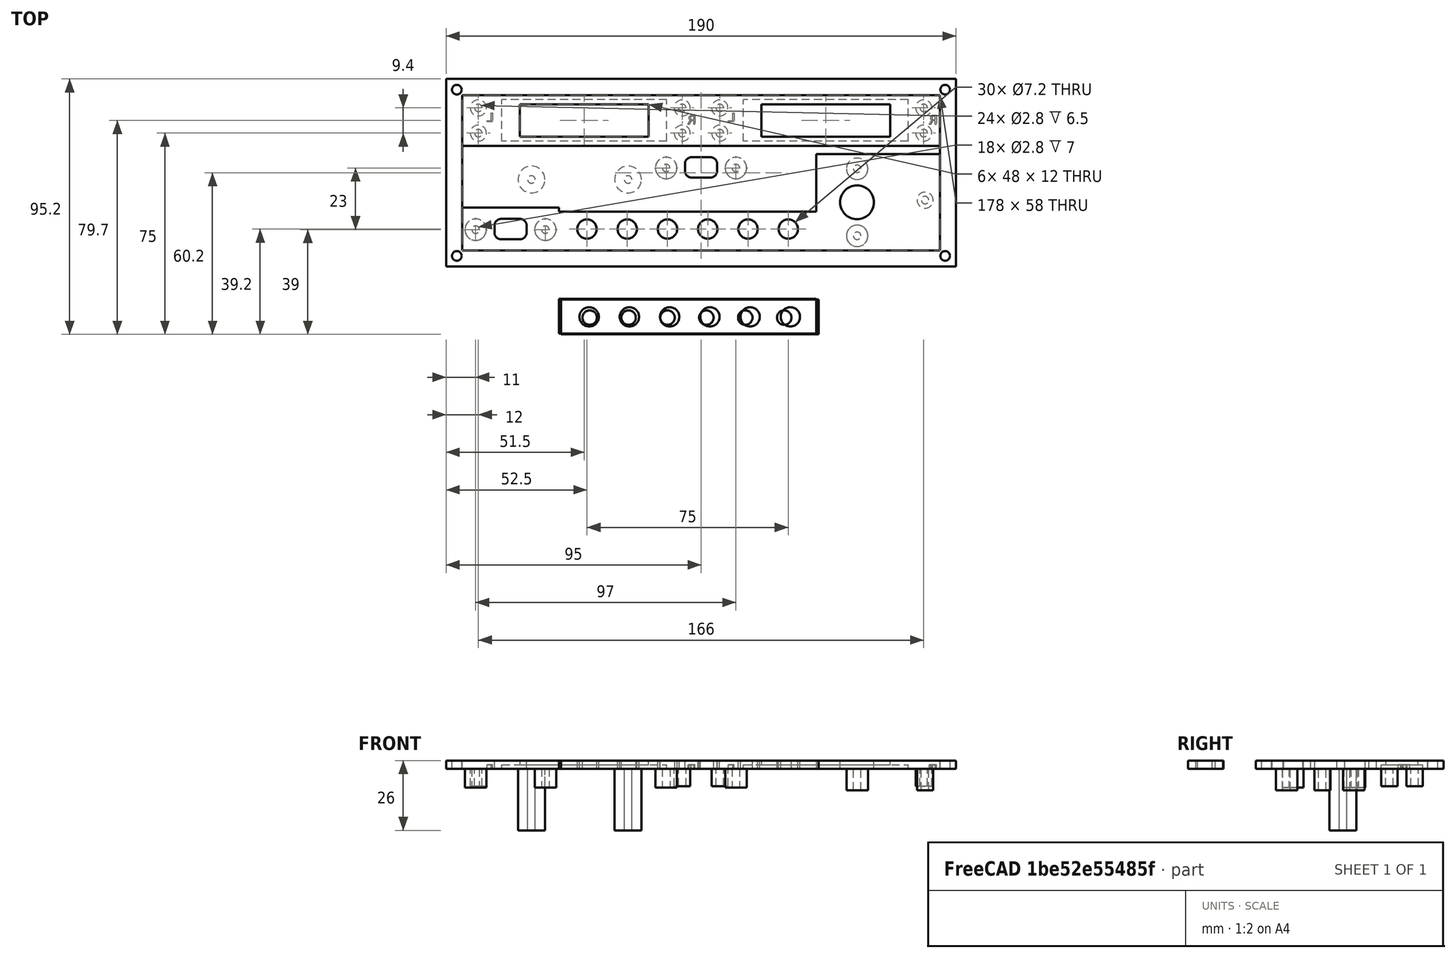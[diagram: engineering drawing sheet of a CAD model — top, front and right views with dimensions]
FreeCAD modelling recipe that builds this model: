
FCSTD DOCUMENT  (FreeCAD 0.18.3R)
Label: radio_led_chico
License: All rights reserved
LicenseURL: http://en.wikipedia.org/wiki/All_rights_reserved
objects: Part::Box×16, Part::Feature×16, Part::Cut×12, Part::Cylinder×10, Part::MultiFuse×10, TechDraw::DrawSVGTemplate×1, TechDraw::DrawViewPart×1, TechDraw::DrawPage×1
note: 64 computed .brp shape members not serialized (recipe doc carries the construction recipe); baked Part::Feature solids carry a one-line shape summary decoded from their .brp

FEATURE [Part::Box] Box  label="Cube"
  AttacherType = Attacher::AttachEngine3D
  Height = 3
  Length = 190
  Width = 70
FEATURE [Part::Box] Box001  label="Cube001"
  AttacherType = Attacher::AttachEngine3D
  Height = 3
  Length = 178
  Placement = pos=(6,6,0) rot=(0,0,1;0rad)
  Width = 58
FEATURE [Part::Cut] Cut  label="marco"
  Base = -> Box
  Placement = pos=(-89,19,-107) rot=(0,0,1;0rad)
  Tool = -> Box001
FEATURE [Part::Box] Box002  label="Cube002"
  AttacherType = Attacher::AttachEngine3D
  Height = 3
  Length = 96
  Placement = pos=(-47,25,3) rot=(0,0,1;0rad)
  Width = 13
FEATURE [Part::Cylinder] Cylinder
  Angle = 360
  AttacherType = Attacher::AttachEngine3D
  Height = 10
  Placement = pos=(-35.5,31,0) rot=(0,0,1;0rad)
  Radius = 2.7
FEATURE [Part::Cylinder] Cylinder001 .. Cylinder005  x5 (patterned run collapsed; names and placements below)
  Angle = 360
  AttacherType = Attacher::AttachEngine3D
  Height = 10
  Radius = 2.7
  placements: 5 in arithmetic series — first pos=(-21,31,0) rot=(0,0,1;0rad), step (14.5,0,0), last pos=(37,31,0) rot=(0,0,1;0rad)
FEATURE [Part::Cut] Cut001001001002003001008002002033001001001001001001001002001001002001045002003017008007003
  Base = -> Box002
  Tool = -> Cylinder005
FEATURE [Part::Cut] Cut001001001002003001008002002033001001001001001001001002001001002001045002003017008007004
  Base = -> Cut001001001002003001008002002033001001001001001001001002001001002001045002003017008007003
  Tool = -> Cylinder004
FEATURE [Part::Cut] Cut001001001002003001008002002033001001001001001001001002001001002001045002003017008007005
  Base = -> Cut001001001002003001008002002033001001001001001001001002001001002001045002003017008007004
  Tool = -> Cylinder003
FEATURE [Part::Cut] Cut001001001002003001008002002033001001001001001001001002001001002001045002003017008007006
  Base = -> Cut001001001002003001008002002033001001001001001001001002001001002001045002003017008007005
  Tool = -> Cylinder002
FEATURE [Part::Cut] Cut001001001002003001008002002033001001001001001001001002001001002001045002003017008007007
  Base = -> Cut001001001002003001008002002033001001001001001001001002001001002001045002003017008007006
  Tool = -> Cylinder001
FEATURE [Part::Cut] Cut001001001002003001008002002033001001001001001001001002001001002001045002003017008007008  label="6leds_6mm_diametro"
  Base = -> Cut001001001002003001008002002033001001001001001001001002001001002001045002003017008007007
  Placement = pos=(0,-31,-110) rot=(0,0,1;0rad)
  Tool = -> Cylinder
FEATURE [Part::Box] Box003  label="Cube003"
  AttacherType = Attacher::AttachEngine3D
  Height = 3
  Length = 71
  Placement = pos=(-83,38,-107) rot=(0,0,1;0rad)
  Width = 26
FEATURE [Part::Box] Box004  label="Cube004"
  AttacherType = Attacher::AttachEngine3D
  Height = 3
  Length = 36
  Placement = pos=(-12,38,-107) rot=(0,0,1;0rad)
  Width = 13
FEATURE [Part::Box] Box005  label="Cube005"
  AttacherType = Attacher::AttachEngine3D
  Height = 3
  Length = 25
  Placement = pos=(24,38,-107) rot=(0,0,1;0rad)
  Width = 26
FEATURE [Part::Box] Box006  label="relleno2"
  AttacherType = Attacher::AttachEngine3D
  Height = 3
  Length = 2
  Placement = pos=(5,64,-107) rot=(0,0,1;0rad)
  Width = 19
FEATURE [Part::Box] Box007  label="Cube007"
  AttacherType = Attacher::AttachEngine3D
  Height = 3
  Length = 46
  Placement = pos=(49,61,-107) rot=(0,0,1;0rad)
  Width = 3
FEATURE [Part::MultiFuse] Fusion
  Shapes = -> [Box003,Box004]
FEATURE [Part::MultiFuse] Fusion007002009027003
  Shapes = -> [Fusion,Box005]
FEATURE [Part::Cylinder] Cylinder006
  Angle = 360
  AttacherType = Attacher::AttachEngine3D
  Height = 10
  Placement = pos=(-85,23,-111) rot=(0,0,1;0rad)
  Radius = 1.8
FEATURE [Part::Cylinder] Cylinder007
  Angle = 360
  AttacherType = Attacher::AttachEngine3D
  Height = 10
  Placement = pos=(-85,85,-113) rot=(0,0,1;0rad)
  Radius = 1.8
FEATURE [Part::Cylinder] Cylinder008
  Angle = 360
  AttacherType = Attacher::AttachEngine3D
  Height = 10
  Placement = pos=(97,23,-111) rot=(0,0,1;0rad)
  Radius = 1.8
FEATURE [Part::Cylinder] Cylinder009
  Angle = 360
  AttacherType = Attacher::AttachEngine3D
  Height = 10
  Placement = pos=(97,85,-111) rot=(0,0,1;0rad)
  Radius = 1.8
FEATURE [Part::Cut] Cut001001001002003001008002002033001001001001001001001002001001002001045002003017008007009
  Base = -> Cut
  Tool = -> Cylinder006
FEATURE [Part::Cut] Cut001001001002003001008002002033001001001001001001001002001001002001045002003017008007010
  Base = -> Cut001001001002003001008002002033001001001001001001001002001001002001045002003017008007009
  Tool = -> Cylinder007
FEATURE [Part::Cut] Cut001001001002003001008002002033001001001001001001001002001001002001045002003017008007011
  Base = -> Cut001001001002003001008002002033001001001001001001001002001001002001045002003017008007010
  Tool = -> Cylinder009
FEATURE [Part::Cut] Cut001001001002003001008002002033001001001001001001001002001001002001045002003017008007012  label="marco_con_agujeros"
  Base = -> Cut001001001002003001008002002033001001001001001001001002001001002001045002003017008007011
  Tool = -> Cylinder008
FEATURE [Part::Box] Box008  label="Cube008"
  AttacherType = Attacher::AttachEngine3D
  Height = 3
  Length = 96
  Placement = pos=(-47,25,-107) rot=(0,0,1;0rad)
  Width = 3
FEATURE [Part::MultiFuse] Fusion007002009027003005008003003014  label="soporte_alto_1"
  Placement = pos=(-164,36,0) rot=(0,0,1;0rad)
FEATURE [Part::MultiFuse] Fusion007002009027003005008003003006005002  label="soporte_alto_2"
  Placement = pos=(-128,36,0) rot=(0,0,1;0rad)
FEATURE [Part::Feature] Cut001001001002003001008002002033001001001001001001001002001001002001045002003017008007002010007002014003004001  label="base_boton_bajo_16x038_selector"
  Placement = pos=(-117,37,0) rot=(0,0,1;0rad)
  shape: bbox 36 x 16 x 10 mm, 26 faces (baked)
FEATURE [Part::Feature] Cut001001001002003001008002002033001001001001001001001002001001002001045002003017008007002010007002014003004002  label="base_boton_bajo_16x039_switch"
  Placement = pos=(-46,60,0) rot=(0,0,1;0rad)
  shape: bbox 36 x 16 x 10 mm, 26 faces (baked)
FEATURE [Part::Feature] Cut001001001002003001008002002033001001001001001001001002001001002001045002003017008007002010007002014003013001  label="base_7seg_full_3mm_88x021_stby"
  Placement = pos=(2,0,0) rot=(0,0,1;0rad)
  shape: bbox 88 x 19 x 9.5 mm, 63 faces (baked)
FEATURE [Part::Feature] Cut001001001002003001008002002033001001001001001001001002001001002001045002003017008007002010007002014003013002  label="base_7seg_full_3mm_88x022_act"
  Placement = pos=(-88,0,0) rot=(0,0,1;0rad)
  shape: bbox 88 x 19 x 9.5 mm, 63 faces (baked)
FEATURE [Part::Feature] Fusion007002009027003005008003003018001  label="base_encoder_doble_46x36_agujero_13"
  Placement = pos=(102.5,-18,0) rot=(0,0,1;0rad)
  shape: bbox 46 x 36 x 11 mm, 19 faces (baked)
FEATURE [Part::Feature] Cut001001001002003001008002002033001001001001001001001002001001002001045002003017008007002010007002014003018001  label="base_led_radius_36_ref"
  Placement = pos=(-57,-22,0) rot=(0,0,1;0rad)
  shape: bbox 10.6 x 10.6 x 3 mm, 7 faces (baked)
FEATURE [Part::Feature] Cut001001001002003001008002002033001001001001001001001002001001002001045002003017008007002010007002014003018002  label="base_led_radius_36_ref001"
  Placement = pos=(-42,-22,0) rot=(0,0,1;0rad)
  shape: bbox 10.6 x 10.6 x 3 mm, 7 faces (baked)
FEATURE [Part::Feature] Cut001001001002003001008002002033001001001001001001001002001001002001045002003017008007002010007002014003018003  label="base_led_radius_36_ref002"
  Placement = pos=(-27,-22,0) rot=(0,0,1;0rad)
  shape: bbox 10.6 x 10.6 x 3 mm, 7 faces (baked)
FEATURE [Part::Feature] Cut001001001002003001008002002033001001001001001001001002001001002001045002003017008007002010007002014003018004  label="base_led_radius_36_ref003"
  Placement = pos=(-12,-22,0) rot=(0,0,1;0rad)
  shape: bbox 10.6 x 10.6 x 3 mm, 7 faces (baked)
FEATURE [Part::Feature] Cut001001001002003001008002002033001001001001001001001002001001002001045002003017008007002010007002014003018005  label="base_led_radius_36_ref004"
  Placement = pos=(3,-22,0) rot=(0,0,1;0rad)
  shape: bbox 10.6 x 10.6 x 3 mm, 7 faces (baked)
FEATURE [Part::Feature] Cut001001001002003001008002002033001001001001001001001002001001002001045002003017008007002010007002014003018006  label="base_led_radius_36_ref005"
  Placement = pos=(18,-22,0) rot=(0,0,1;0rad)
  shape: bbox 10.6 x 10.6 x 3 mm, 7 faces (baked)
FEATURE [Part::Box] Box009  label="Cube009"
  AttacherType = Attacher::AttachEngine3D
  Height = 3
  Length = 7
  Placement = pos=(-32,-5,-107) rot=(0,0,1;0rad)
  Width = 10.6
FEATURE [Part::Box] Box010  label="Cube010"
  AttacherType = Attacher::AttachEngine3D
  Height = 3
  Length = 7
  Placement = pos=(-17,-5,-107) rot=(0,0,1;0rad)
  Width = 10.6
FEATURE [Part::Box] Box011  label="Cube011"
  AttacherType = Attacher::AttachEngine3D
  Height = 3
  Length = 7
  Placement = pos=(-2,-5,-107) rot=(0,0,1;0rad)
  Width = 10.6
FEATURE [Part::Box] Box012  label="Cube012"
  AttacherType = Attacher::AttachEngine3D
  Height = 3
  Length = 7
  Placement = pos=(13,-5,-107) rot=(0,0,1;0rad)
  Width = 10.6
FEATURE [Part::Box] Box013  label="Cube013"
  AttacherType = Attacher::AttachEngine3D
  Height = 3
  Length = 7
  Placement = pos=(28,-5,-107) rot=(0,0,1;0rad)
  Width = 10.6
FEATURE [Part::Box] Box014  label="Cube014"
  AttacherType = Attacher::AttachEngine3D
  Height = 3
  Length = 96
  Placement = pos=(-46.2,-6.2,-107) rot=(0,0,1;0rad)
  Width = 13
FEATURE [Part::MultiFuse] Fusion007002009027003005008003003006005003
  Shapes = -> [Cut001001001002003001008002002033001001001001001001001002001001002001045002003017008007002010007002014003018001,Box009,Cut001001001002003001008002002033001001001001001001001002001001002001045002003017008007002010007002014003018002,Box010,Cut001001001002003001008002002033001001001001001001001002001001002001045002003017008007002010007002014003018003,Box011,+5 more]
FEATURE [Part::Box] Box015  label="Cube015"
  AttacherType = Attacher::AttachEngine3D
  Height = 3
  Length = 84
  Placement = pos=(-40.2,-4.8,-107) rot=(0,0,1;0rad)
  Width = 10.4
FEATURE [Part::Cut] Cut001001001002003001008002002033001001001001001001001002001001002001045002003017008007002010007002014003018007
  Base = -> Box014
  Tool = -> Box015
FEATURE [Part::MultiFuse] Fusion007002009027003005008003003006005004
  Shapes = -> [Fusion007002009027003005008003003006005003,Cut001001001002003001008002002033001001001001001001001002001001002001045002003017008007002010007002014003018007]
FEATURE [Part::Feature] Fusion007002009027003005008003003006005004001  label="6_leds_chicos"
  Placement = pos=(-0.8,32.7,0) rot=(0,0,1;0rad)
  shape: bbox 96 x 13 x 3 mm, 12 faces (baked)
FEATURE [Part::MultiFuse] Fusion007002009027003005008003003006005004002
  Shapes = -> [Fusion007002009027003005008003003006005004001,Box008,Cut001001001002003001008002002033001001001001001001001002001001002001045002003017008007002010007002014003004001,Fusion007002009027003005008003003018001]
FEATURE [Part::Feature] Fusion007002009027003005008003003006005004002001  label="Fusion007002009027003005008003003006005004003"
  shape: bbox 178 x 36 x 11 mm, 45 faces (baked)
FEATURE [Part::MultiFuse] Fusion007002009027003005008003003006005004002002
  Shapes = -> [Fusion007002009027003005008003003006005004002001,Fusion007002009027003,Box007,Cut001001001002003001008002002033001001001001001001001002001001002001045002003017008007002010007002014003004002]
FEATURE [Part::Feature] Fusion007002009027003005008003003006005004002002001  label="Fusion007002009027003005008003003006005004002003"
  shape: bbox 178 x 39 x 11 mm, 57 faces (baked)
FEATURE [Part::MultiFuse] Fusion007002009027003005008003003006005004002002002
  Shapes = -> [Fusion007002009027003005008003003006005004002002001,Box006,Cut001001001002003001008002002033001001001001001001001002001001002001045002003017008007002010007002014003013002,Cut001001001002003001008002002033001001001001001001001002001001002001045002003017008007002010007002014003013001]
FEATURE [Part::Feature] Fusion007002009027003005008003003006005004002002002001  label="Fusion007002009027003005008003003006005004002002003"
  shape: bbox 178 x 58 x 11 mm, 171 faces (baked)
FEATURE [Part::MultiFuse] Fusion007002009027003005008003003006005004002002002002
  Shapes = -> [Fusion007002009027003005008003003006005004002002002001,Cut001001001002003001008002002033001001001001001001001002001001002001045002003017008007012,Fusion007002009027003005008003003014,Fusion007002009027003005008003003006005002]
FEATURE [Part::Feature] Fusion007002009027003005008003003006005004002002002002001  label="radio_con_leds_chicos"
  shape: bbox 190 x 70 x 26 mm, 183 faces (baked)
FEATURE [TechDraw::DrawSVGTemplate] Template
  Height = 297
  Orientation = 1
  Width = 420
FEATURE [TechDraw::DrawViewPart] View
  CoarseView = true
  Direction = (0,0,1)
  Focus = 100
  HardHidden = false
  IsoCount = 0
  IsoHidden = false
  IsoVisible = true
  LockPosition = false
  Perspective = false
  Rotation = 0
  ScaleType = 0
  SeamHidden = false
  SeamVisible = true
  SmoothHidden = false
  SmoothVisible = true
  Source = -> [Fusion007002009027003005008003003006005004002002002002001]
  X = 210
  Y = 148.5
FEATURE [TechDraw::DrawPage] Page
  KeepUpdated = true
  ProjectionType = 0
  Template = -> Template
  Views = -> [View]
